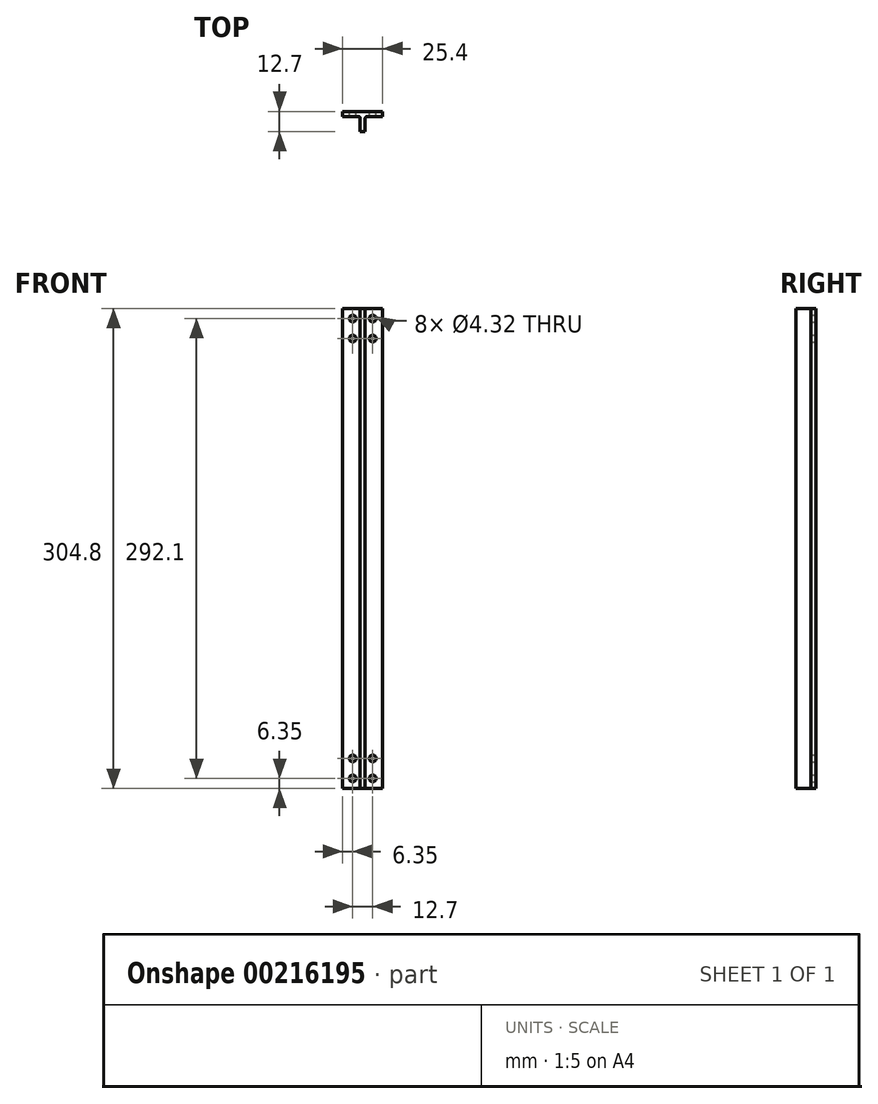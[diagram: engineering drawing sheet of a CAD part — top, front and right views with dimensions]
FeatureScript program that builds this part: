
annotation { "Feature Type Name" : "Feature", "Feature Type Description" : "" }
export const myFeature = defineFeature(function(context is Context, id is Id, definition is map)
    precondition{}
    {
        {
            var Q0;
            Q0=qCreatedBy(makeId("Top.planeOp"),FACE);
            var sketch = newSketch(context, id + "F0", { "sketchPlane" : qUnion([Q0])});
            skLineSegment(sketch, "E0", {"start": v(0, 0) * mm, "end": v(12.7, 0) * mm});
            skLineSegment(sketch, "E1", {"start": v(12.7, 0) * mm, "end": v(12.7, -3.18) * mm});
            skLineSegment(sketch, "E2", {"start": v(12.7, -3.18) * mm, "end": v(1.59, -3.18) * mm});
            skLineSegment(sketch, "E3", {"start": v(1.59, -3.18) * mm, "end": v(1.59, -12.7) * mm});
            skLineSegment(sketch, "E4", {"start": v(1.59, -12.7) * mm, "end": v(0, -12.7) * mm});
            skLineSegment(sketch, "E5.MirrorCS", {"start": v(-1.59, -12.7) * mm, "end": v(0, -12.7) * mm});
            skLineSegment(sketch, "E6.MirrorCS", {"start": v(-12.7, -3.18) * mm, "end": v(-1.59, -3.18) * mm});
            skLineSegment(sketch, "E7.MirrorCS", {"start": v(-1.59, -3.18) * mm, "end": v(-1.59, -12.7) * mm});
            skLineSegment(sketch, "E8.MirrorCS", {"start": v(0, 0) * mm, "end": v(-12.7, 0) * mm});
            skLineSegment(sketch, "E9.MirrorCS", {"start": v(-12.7, 0) * mm, "end": v(-12.7, -3.18) * mm});
            skSolve(sketch);
        }
        {
            var Q0;
            Q0=qSketchRegion(id+"F0",true);
            extrude(context, id + "F1", {"entities" : qUnion([Q0]), "depth" : 304.8 * mm});
        }
        {
            var Q0;
            Q0=makeQuery(id+"F1.opExtrude","SWEPT_EDGE",EDGE,{"disambiguationData":[OSD([sQuery(id+"F0.wireOp",EDGE,"E6.MirrorCS"),sQuery(id+"F0.wireOp",EDGE,"E7.MirrorCS")])]});
            var Q1;
            Q1=makeQuery(id+"F1.opExtrude","SWEPT_EDGE",EDGE,{"disambiguationData":[OSD([sQuery(id+"F0.wireOp",EDGE,"E2"),sQuery(id+"F0.wireOp",EDGE,"E3")])]});
            fillet(context, id + "F2", {"entities" : qUnion([Q0, Q1]), "radius" : 1.27 * mm, "tangentPropagation" : true, "allowEdgeOverflow" : false});
        }
        {
            var Q0;
            Q0=makeQuery(id+"F1.opExtrude","SWEPT_FACE",FACE,{"disambiguationData":[OSD([sQuery(id+"F0.wireOp",EDGE,"E0"),sQuery(id+"F0.wireOp",EDGE,"E8.MirrorCS")])]});
            var sketch = newSketch(context, id + "F3", { "sketchPlane" : qUnion([Q0])});
            skLineSegment(sketch, "E10", {"start": v(-12.7, 304.8) * mm, "end": v(0, 304.8) * mm});
            skLineSegment(sketch, "E11", {"start": v(0, 304.8) * mm, "end": v(0, 298.45) * mm});
            skLineSegment(sketch, "E12", {"start": v(0, 298.45) * mm, "end": v(0, 285.75) * mm});
            skLineSegment(sketch, "E13", {"start": v(0, 285.75) * mm, "end": v(-12.7, 285.75) * mm});
            skLineSegment(sketch, "E14", {"start": v(-12.7, 285.75) * mm, "end": v(-6.35, 285.75) * mm});
            skLineSegment(sketch, "E15", {"start": v(-6.35, 285.75) * mm, "end": v(-6.35, 298.45) * mm});
            skLineSegment(sketch, "E16.MirrorCS", {"start": v(6.35, 285.75) * mm, "end": v(6.35, 298.45) * mm});
            skLineSegment(sketch, "E17", {"start": v(-12.7, 152.4) * mm, "end": v(12.7, 152.4) * mm});
            skLineSegment(sketch, "E18.MirrorCS", {"start": v(-6.35, 19.05) * mm, "end": v(-6.35, 6.35) * mm});
            skLineSegment(sketch, "E19.MirrorCS", {"start": v(0, 19.05) * mm, "end": v(-12.7, 19.05) * mm});
            skLineSegment(sketch, "E20.MirrorCS", {"start": v(0, 6.35) * mm, "end": v(0, 19.05) * mm});
            skLineSegment(sketch, "E21.MirrorCS", {"start": v(-12.7, 19.05) * mm, "end": v(-6.35, 19.05) * mm});
            skLineSegment(sketch, "E22.MirrorCS", {"start": v(0, 0) * mm, "end": v(0, 6.35) * mm});
            skLineSegment(sketch, "E23.MirrorCS", {"start": v(6.35, 19.05) * mm, "end": v(6.35, 6.35) * mm});
            skLineSegment(sketch, "E24.MirrorCS", {"start": v(-12.7, 0) * mm, "end": v(0, 0) * mm});
            skSolve(sketch);
        }
        {
            var Q0;
            Q0=sQuery(id+"F3.wireOp",VERTEX,"E15.end");
            var Q1;
            Q1=sQuery(id+"F3.wireOp",VERTEX,"E15.start");
            var Q2;
            Q2=sQuery(id+"F3.wireOp",VERTEX,"E16.MirrorCS.start");
            var Q3;
            Q3=sQuery(id+"F3.wireOp",VERTEX,"E16.MirrorCS.end");
            var Q4;
            Q4=sQuery(id+"F3.wireOp",VERTEX,"E18.MirrorCS.end");
            var Q5;
            Q5=sQuery(id+"F3.wireOp",VERTEX,"E21.MirrorCS.end");
            var Q6;
            Q6=sQuery(id+"F3.wireOp",VERTEX,"E23.MirrorCS.start");
            var Q7;
            Q7=sQuery(id+"F3.wireOp",VERTEX,"E23.MirrorCS.end");
            var Q8;
            Q8=makeQuery(id+"F1.opExtrude","SWEPT_BODY",BODY,{"disambiguationData":[OSD([sQuery(id+"F0.wireOp",EDGE,"E0"),sQuery(id+"F0.wireOp",EDGE,"E1"),sQuery(id+"F0.wireOp",EDGE,"E2"),sQuery(id+"F0.wireOp",EDGE,"E3"),sQuery(id+"F0.wireOp",EDGE,"E4"),sQuery(id+"F0.wireOp",EDGE,"E5.MirrorCS"),sQuery(id+"F0.wireOp",EDGE,"E6.MirrorCS"),sQuery(id+"F0.wireOp",EDGE,"E7.MirrorCS"),sQuery(id+"F0.wireOp",EDGE,"E8.MirrorCS"),sQuery(id+"F0.wireOp",EDGE,"E9.MirrorCS")])]});
            hole(context, id + "F4", {"style" : HoleStyle.SIMPLE, "endStyle" : HoleEndStyle.BLIND, "standardTappedOrClearance" : lookupTablePath({ "standard" : "ANSI", "fit" : "Close", "size" : "#8", "type" : "Clearance" }), "standardBlindInLast" : lookupTablePath({ "fit" : "Close", "standard" : "ANSI", "size" : "#8", "type" : "Clearance" }), "holeDiameter" : 4.32 * mm, "holeDepth" : 25.4 * mm, "locations" : qUnion([Q0, Q1, Q2, Q3, Q4, Q5, Q6, Q7]), "scope" : qUnion([Q8])});
        }
    });
